# Revit family: Plymold-Aurora-Bench
name_source: partatom
category: Furniture
units: mm (PartAtom-declared; Revit-internal decimal feet)

## family parameters
Always vertical = Yes
Cut with Voids When Loaded = No
OmniClass Number = 23.40.20.00
OmniClass Title = General Furniture and Specialties
Render Appearance Source = Family Geometry
Room Calculation Point = No
Shared = Yes
Work Plane-Based = No

## types (2) — shared parameters
Assembly Code = E2020200
Default Elevation = 0"
Depth = 19"
GLIDE MATERIAL = PLY - Plastic Black
Height = 18"
Keynote = 12500
Manufacturer = Plymold Inc.
Product Documentation Link = https://plymold.com
Revit Model Built By = https://www.servex-us.com
Sustainability = https://plymold.com
TOP MATERIAL = PLY - Sand
Type Comments = Aurora
URL = https://plymold.com
Width = 57"

## per-type parameters (varying)
| type | Description | FRAME MATERIAL |
| 666457PL03 | Outdoor Bench - Onyx Black - 57"W x 19"D x 18"H | PLY - Onyx Black Powdercoat |
| 666457PL02 | Outdoor Bench - Iron Glimme - 57"W x 19"D x 18"H | PLY - Iron Glimme Powdercoat |

note: column(s) folded — value = type name in every type: Model

## geometry (parser evidence)
native form markers: Sweep x2
no freeform markers — native parametric forms only
